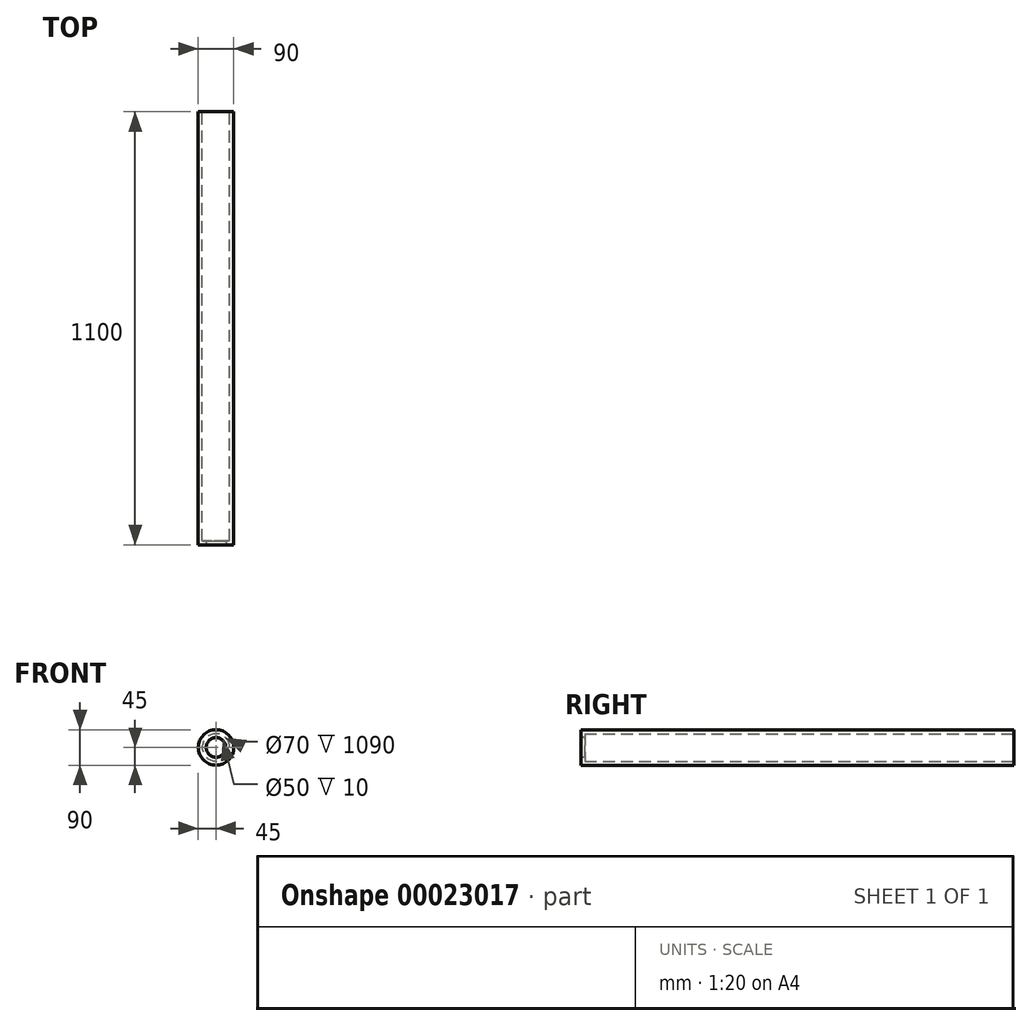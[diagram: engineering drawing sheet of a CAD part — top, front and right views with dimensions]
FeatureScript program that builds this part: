
annotation { "Feature Type Name" : "Feature", "Feature Type Description" : "" }
export const myFeature = defineFeature(function(context is Context, id is Id, definition is map)
    precondition{}
    {
        {
            var Q0;
            Q0=qCreatedBy(makeId("Front.planeOp"),FACE);
            var sketch = newSketch(context, id + "F0", { "sketchPlane" : qUnion([Q0])});
            skCircle(sketch, "E0", {"center": v(0, 0) * mm, "radius": 45 * mm});
            skSolve(sketch);
        }
        {
            var Q0;
            Q0 = qSketchRegion(id + "F0", true);
            extrude(context, id + "F1", {"entities" : qUnion([Q0]), "oppositeDirection" : true, "depth" : 1100 * mm});
        }
        {
            var Q0;
            Q0=makeQuery(id+"F1.opExtrude","CAP_FACE",FACE,{"disambiguationData":[OSD([sQuery(id+"F0.wireOp",EDGE,"E0")])],"isStart":false});
            var sketch = newSketch(context, id + "F2", { "sketchPlane" : qUnion([Q0])});
            skCircle(sketch, "E1", {"center": v(0, 0) * mm, "radius": 35 * mm});
            skSolve(sketch);
        }
        {
            var Q0;
            Q0 = qSketchRegion(id + "F2", true);
            extrude(context, id + "F3", {"entities" : qUnion([Q0]), "operationType" : NewBodyOperationType.REMOVE, "oppositeDirection" : true, "depth" : 1000 * mm});
        }
        {
            var Q0;
            Q0 = qSketchRegion(id + "F2", true);
            extrude(context, id + "F4", {"entities" : qUnion([Q0]), "operationType" : NewBodyOperationType.REMOVE, "oppositeDirection" : true, "depth" : 1090 * mm});
        }
        {
            var Q0;
            Q0=makeQuery(id+"F1.opExtrude","CAP_FACE",FACE,{"disambiguationData":[OSD([sQuery(id+"F0.wireOp",EDGE,"E0")])],"isStart":true});
            var sketch = newSketch(context, id + "F5", { "sketchPlane" : qUnion([Q0])});
            skCircle(sketch, "E2", {"center": v(0, 0) * mm, "radius": 25 * mm});
            skSolve(sketch);
        }
        {
            var Q0;
            Q0=makeQuery(id+"F5.imprint","IMPRINT",FACE,{"disambiguationData":[TD([[makeQuery(id+"F5.imprint","IMPRINT",EDGE,{"derivedFrom":sQuery(id+"F5.wireOp",EDGE,"E2")}),1.0]])]});
            extrude(context, id + "F6", {"entities" : qUnion([Q0]), "operationType" : NewBodyOperationType.REMOVE, "oppositeDirection" : true, "depth" : 10 * mm});
        }
    });
